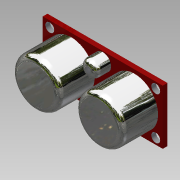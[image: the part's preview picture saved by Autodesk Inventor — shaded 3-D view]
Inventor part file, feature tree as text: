
AUTODESK INVENTOR PART (.ipt)
format: ipt  version: 2015 SP1 (Build 190203100, 203)  size: 203,264 bytes
history: native  units: mm
features: extrude x6, sketch x3, fillet x2
ambient origin geometry x8: Origin, YZ Plane, XZ Plane, XY Plane, X Axis, Y Axis, Z Axis, Center Point
bodies: Solid1 (feature_tree)
feature tree (11):
  sketch  "Sketch1"  dims[d0=43.21mm d1=19.7mm]
  extrude  "Extrusion1"  Depth=19.7mm
  extrude  "Extrusion2"  Depth=3.2mm
  extrude  "Extrusion3"  Depth=10.0mm
  extrude  "Extrusion4"  Depth=10.0mm
  extrude  "Extrusion5"  Depth=1.7mm TaperAngle=0.0deg
  fillet  "Fillet1"  Radius=14.6mm
  fillet  "Fillet2"  Radius=7.07mm
  extrude  "Extrusion6"  Depth=5.2mm
  sketch  "Sketch3"  dims[d8=17.0mm d9=17.0mm d14=6.0mm d16=1.7mm d17=0.0mm d18=14.6mm d19=0.0mm d20=7.07mm d21=0.0mm d22=5.2mm d23=10.13mm d24=2.0mm d25=0.0mm d26=1.27mm d27=1.27mm d28=1.27mm d29=1.27mm d30=1.27mm d31=2.54mm d32=2.54mm d33=2.54mm d34=2.54mm d35=2.0mm d36=0.0mm d37=2.0mm d38=2.0mm d41=22.86mm d43=10.175mm d44=10.175mm d45=6.54mm d47=7.874mm d48=7.654mm d49=7.654mm d50=7.654mm d51=7.654mm d52=90.0deg d53=180.0deg d54=10.0mm d55=0.0mm d56=2.196mm]
  sketch  "Sketch2"  dims[d2=3.2mm d5=3.2mm]
